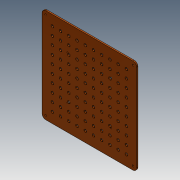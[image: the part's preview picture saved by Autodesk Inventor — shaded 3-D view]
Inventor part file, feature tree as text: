
AUTODESK INVENTOR PART (.ipt)
format: ipt  version: 2018.3 (Build 223284000, 284)  size: 533,504 bytes
history: native  units: in
note: dims shown in document units (in); Inventor stores cm internally (conversion verified against a paired STEP export)
features: extrude x2, hole x2, fillet x1, pattern_linear x1, sketch x1
ambient origin geometry x8: Origin, YZ Plane, XZ Plane, XY Plane, X Axis, Y Axis, Z Axis, Center Point
bodies: Solid1 (feature_tree)
feature tree (7):
  extrude  "Extrusion1"  Depth=5.085in
  fillet  "Fillet2"  Radius=13.0in
  hole  "Hole6"  [1 undecoded]
  hole  "Hole10"  [1 undecoded]
  extrude  "Extrusion4"  Depth=4.52in
  pattern_linear  "Rectangular Pattern3"  Spacing1=0.5in  [1 undecoded]
  sketch  "Sketch4"  dims[d0=5.085in d1=5.085in d2=13.0in d4=0.18in d5=0.0in d23=6.0in d36=4.52in d50=0.5in d63=12.0in d64=0.255in d65=0.5in d83=0.25in d84=0.472in d85=0.375in d86=0.25in d87=0.5635in d88=1.0in d89=0.8108in d97=1.29in d98=45.0deg d99=30.0deg d100=1.13in d115=0.185in d116=0.472in d117=0.409in d118=0.25in d119=90.0deg d120=0.559in d121=0.8108in d122=0.339in d123=1.0in d124=0.0in d125=3.937in d127=1.13in d128=3.937in d130=1.13in]
note: 3 required parameter values undecoded (feature->parameter linkage not recoverable at this tier; creation-order binding heuristic only, values carry confidence <= 0.55)
